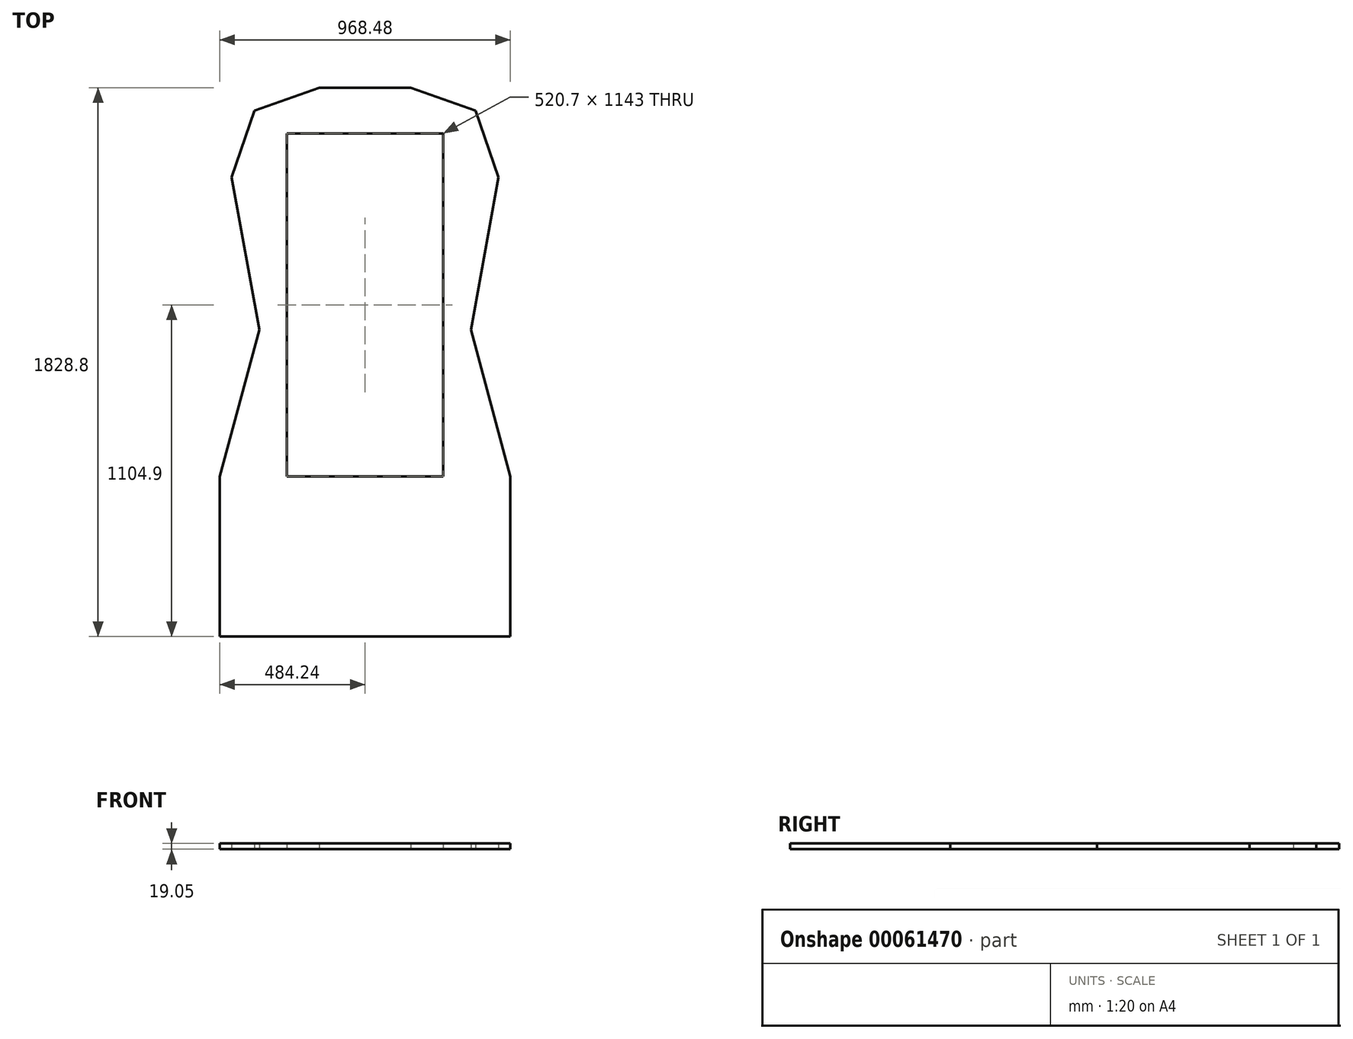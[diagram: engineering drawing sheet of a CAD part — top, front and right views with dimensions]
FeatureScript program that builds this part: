
annotation { "Feature Type Name" : "Feature", "Feature Type Description" : "" }
export const myFeature = defineFeature(function(context is Context, id is Id, definition is map)
    precondition{}
    {
        {
            var Q0;
            Q0=qCreatedBy(makeId("Top.planeOp"),FACE);
            var sketch = newSketch(context, id + "F0", { "sketchPlane" : qUnion([Q0])});
            skLineSegment(sketch, "E0", {"start": v(0, 506.23) * mm, "end": v(0, -822.49) * mm, "construction": true});
            skLineSegment(sketch, "E1", {"start": v(0, 506.23) * mm, "end": v(-152.4, 506.23) * mm});
            skLineSegment(sketch, "E2", {"start": v(-152.4, 506.23) * mm, "end": v(-368.3, 430.03) * mm});
            skLineSegment(sketch, "E3", {"start": v(-368.3, 430.03) * mm, "end": v(-444.5, 207.78) * mm});
            skLineSegment(sketch, "E4", {"start": v(-444.5, 207.78) * mm, "end": v(-352.42, -300.22) * mm});
            skLineSegment(sketch, "E5", {"start": v(-352.42, -300.22) * mm, "end": v(-484.24, -789.17) * mm});
            skLineSegment(sketch, "E6", {"start": v(-484.24, -789.17) * mm, "end": v(-484.24, -1322.57) * mm});
            skLineSegment(sketch, "E7", {"start": v(-484.24, -1322.57) * mm, "end": v(0, -1322.57) * mm});
            skLineSegment(sketch, "E8", {"start": v(0, 353.83) * mm, "end": v(-260.35, 353.83) * mm});
            skLineSegment(sketch, "E9", {"start": v(-260.35, 353.83) * mm, "end": v(-260.35, -789.17) * mm});
            skLineSegment(sketch, "E10", {"start": v(-260.35, -789.17) * mm, "end": v(0, -789.17) * mm});
            skLineSegment(sketch, "E11", {"start": v(0, -789.17) * mm, "end": v(0, -1322.57) * mm});
            skLineSegment(sketch, "E12", {"start": v(0, 506.23) * mm, "end": v(0, 353.83) * mm});
            skLineSegment(sketch, "E13.MirrorCS", {"start": v(0, 506.23) * mm, "end": v(152.4, 506.23) * mm});
            skLineSegment(sketch, "E14.MirrorCS", {"start": v(152.4, 506.23) * mm, "end": v(368.3, 430.03) * mm});
            skLineSegment(sketch, "E15.MirrorCS", {"start": v(368.3, 430.03) * mm, "end": v(444.5, 207.78) * mm});
            skLineSegment(sketch, "E16.MirrorCS", {"start": v(444.5, 207.78) * mm, "end": v(352.42, -300.22) * mm});
            skLineSegment(sketch, "E17.MirrorCS", {"start": v(352.42, -300.22) * mm, "end": v(484.24, -789.17) * mm});
            skLineSegment(sketch, "E18.MirrorCS", {"start": v(0, 353.83) * mm, "end": v(260.35, 353.83) * mm});
            skLineSegment(sketch, "E19.MirrorCS", {"start": v(260.35, 353.83) * mm, "end": v(260.35, -789.17) * mm});
            skLineSegment(sketch, "E20.MirrorCS", {"start": v(260.35, -789.17) * mm, "end": v(0, -789.17) * mm});
            skLineSegment(sketch, "E21.MirrorCS", {"start": v(484.24, -1322.57) * mm, "end": v(0, -1322.57) * mm});
            skLineSegment(sketch, "E22.MirrorCS", {"start": v(484.24, -789.17) * mm, "end": v(484.24, -1322.57) * mm});
            skSolve(sketch);
        }
        {
            var Q0;
            Q0=makeQuery(id+"F0.imprint","IMPRINT",FACE,{"disambiguationData":[TD([[makeQuery(id+"F0.imprint","IMPRINT",EDGE,{"derivedFrom":sQuery(id+"F0.wireOp",EDGE,"E1")}),1.0]])]});
            var Q1;
            Q1=makeQuery(id+"F0.imprint","IMPRINT",FACE,{"disambiguationData":[TD([[makeQuery(id+"F0.imprint","IMPRINT",EDGE,{"derivedFrom":sQuery(id+"F0.wireOp",EDGE,"E11")}),1.0]])]});
            extrude(context, id + "F1", {"entities" : qUnion([Q0, Q1]), "depth" : 19.05 * mm});
        }
    });
